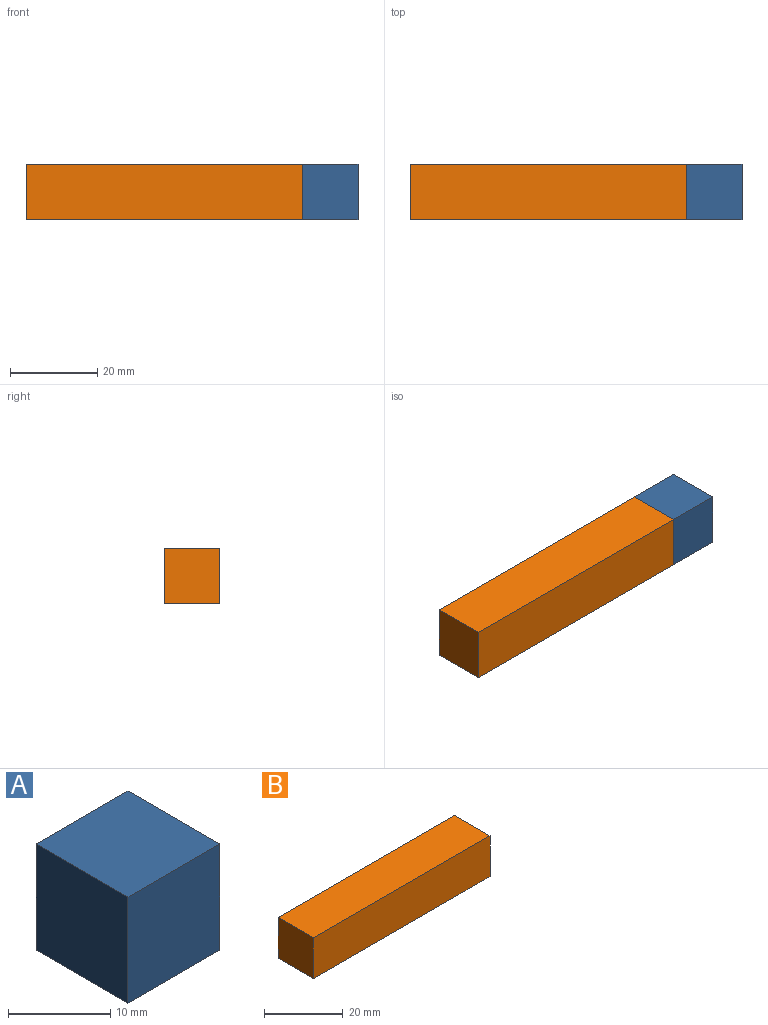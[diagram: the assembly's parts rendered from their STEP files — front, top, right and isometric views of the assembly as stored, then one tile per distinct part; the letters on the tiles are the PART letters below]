
ASSEMBLY  parts=2 mates=1
PART A: 6 faces, bbox 12.7x12.7x12.7 mm
  f0: plane 12.7x12.7mm, normal (0,0,-1), area 161.3mm2, adj f1,f3,f4,f5
  f1: plane 12.7x12.7mm, normal (1,0,0), area 161.3mm2, adj f0,f2,f4,f5
  f2: plane 12.7x12.7mm, normal (0,0,1), area 161.3mm2, adj f1,f3,f4,f5
  f3: plane 12.7x12.7mm, normal (-1,0,0), area 161.3mm2, adj f0,f2,f4,f5
  f4: plane 12.7x12.7mm, normal (0,-1,0), area 161.3mm2, adj f0,f1,f2,f3
  f5: plane 12.7x12.7mm, normal (0,1,0), area 161.3mm2, adj f0,f1,f2,f3
PART B: 6 faces, bbox 63.5x12.7x12.7 mm
  f0: plane 63.5x12.7mm, normal (0,0,-1), area 806.5mm2, adj f1,f3,f4,f5
  f1: plane 12.7x12.7mm, normal (1,0,0), area 161.3mm2, adj f0,f2,f4,f5
  f2: plane 63.5x12.7mm, normal (0,0,1), area 806.5mm2, adj f1,f3,f4,f5
  f3: plane 12.7x12.7mm, normal (-1,0,0), area 161.3mm2, adj f0,f2,f4,f5
  f4: plane 63.5x12.7mm, normal (0,-1,0), area 806.5mm2, adj f0,f1,f2,f3
  f5: plane 63.5x12.7mm, normal (0,1,0), area 806.5mm2, adj f0,f1,f2,f3
PLACE A t=(-7.54,-5.55,-2.24)mm
PLACE B t=(-42.34,-5.55,69.94)mm
MATE fastened B.f1 <-> A.f3  axis (1,0,0) through (-13.89,-11.9,26.33)mm
